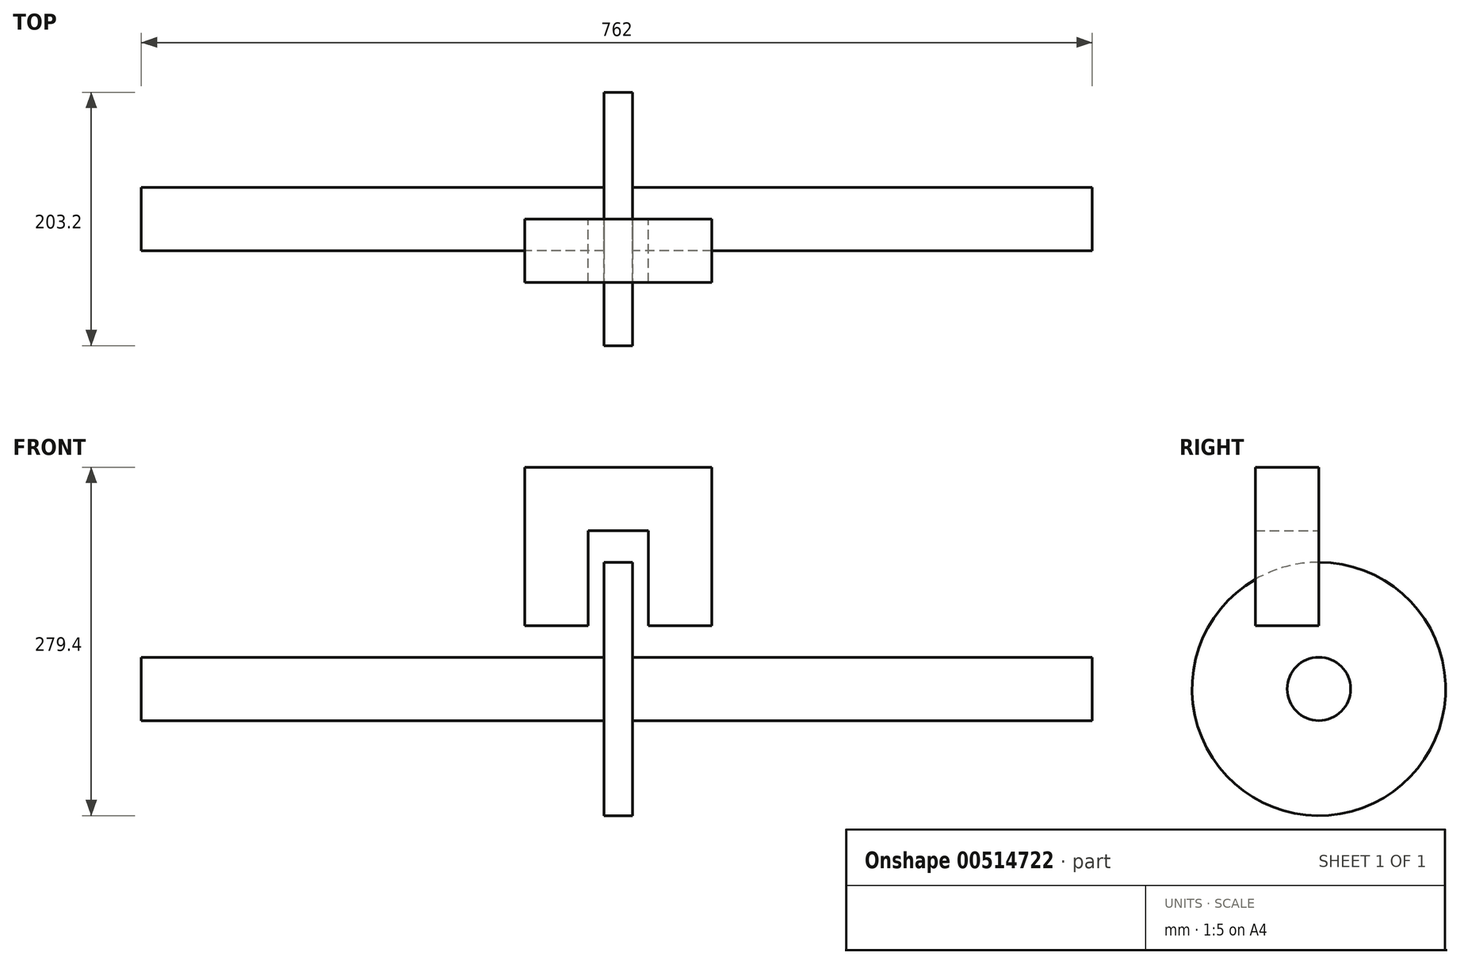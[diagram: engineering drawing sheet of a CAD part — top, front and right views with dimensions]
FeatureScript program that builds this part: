
annotation { "Feature Type Name" : "Feature", "Feature Type Description" : "" }
export const myFeature = defineFeature(function(context is Context, id is Id, definition is map)
    precondition{}
    {
        {
            var Q0;
            Q0=qCreatedBy(makeId("Front.planeOp"),FACE);
            var sketch = newSketch(context, id + "F0", { "sketchPlane" : qUnion([Q0])});
            skLineSegment(sketch, "E0", {"start": v(-381, 20.1) * mm, "end": v(381, 20.1) * mm});
            skLineSegment(sketch, "E1", {"start": v(381, 20.1) * mm, "end": v(381, -5.3) * mm});
            skLineSegment(sketch, "E2", {"start": v(-381, -5.3) * mm, "end": v(-381, 20.1) * mm});
            skLineSegment(sketch, "E3", {"start": v(-381, -5.3) * mm, "end": v(381, -5.3) * mm});
            skPoint(sketch, "E4", {"position": v(0, 20.1) * mm});
            skPoint(sketch, "E5", {"position": v(-10.38, 20.1) * mm});
            skPoint(sketch, "E6", {"position": v(12.7, 20.1) * mm});
            skLineSegment(sketch, "E7", {"start": v(-10.38, 20.1) * mm, "end": v(-10.38, 96.3) * mm});
            skLineSegment(sketch, "E8", {"start": v(-10.38, 96.3) * mm, "end": v(12.7, 96.3) * mm});
            skLineSegment(sketch, "E9", {"start": v(12.7, 96.3) * mm, "end": v(12.7, 20.1) * mm});
            skLineSegment(sketch, "E10", {"start": v(-23.08, 45.5) * mm, "end": v(-23.08, 121.7) * mm});
            skLineSegment(sketch, "E11", {"start": v(-23.08, 121.7) * mm, "end": v(25.4, 121.7) * mm});
            skLineSegment(sketch, "E12", {"start": v(25.4, 121.7) * mm, "end": v(25.4, 45.5) * mm});
            skLineSegment(sketch, "E13", {"start": v(25.4, 45.5) * mm, "end": v(76.2, 45.5) * mm});
            skLineSegment(sketch, "E14", {"start": v(76.2, 45.5) * mm, "end": v(76.2, 172.5) * mm});
            skLineSegment(sketch, "E15", {"start": v(76.2, 172.5) * mm, "end": v(-73.88, 172.5) * mm});
            skLineSegment(sketch, "E16", {"start": v(-73.88, 172.5) * mm, "end": v(-73.88, 45.5) * mm});
            skLineSegment(sketch, "E17", {"start": v(-73.88, 45.5) * mm, "end": v(-23.08, 45.5) * mm});
            skSolve(sketch);
        }
        {
            var Q0;
            {var subQ0=sQuery(id+"F0.wireOp",EDGE,"E1");Q0=makeQuery(id+"F0.imprint","IMPRINT",FACE,{"disambiguationData":[TD([[makeQuery(id+"F0.imprint","IMPRINT",EDGE,{"derivedFrom":subQ0}),-1.0]])]});}
            var Q1;
            {var subQ0=sQuery(id+"F0.wireOp",EDGE,"E7");Q1=makeQuery(id+"F0.imprint","IMPRINT",FACE,{"disambiguationData":[TD([[makeQuery(id+"F0.imprint","IMPRINT",EDGE,{"derivedFrom":subQ0}),-1.0]])]});}
            var Q2;
            Q2=sQuery(id+"F0.wireOp",EDGE,"E3");
            revolve(context, id + "F1", {"entities" : qUnion([Q0, Q1]), "axis" : qUnion([Q2]), "revolveType" : RevolveType.FULL});
        }
        {
            var Q0;
            Q0=makeQuery(id+"F0.imprint","IMPRINT",FACE,{"disambiguationData":[TD([[makeQuery(id+"F0.imprint","IMPRINT",EDGE,{"derivedFrom":sQuery(id+"F0.wireOp",EDGE,"E10")}),1.0]])]});
            extrude(context, id + "F2", {"entities" : qUnion([Q0]), "operationType" : NewBodyOperationType.ADD, "depth" : 50.8 * mm, "offsetDistance" : 25.4 * mm});
        }
    });
